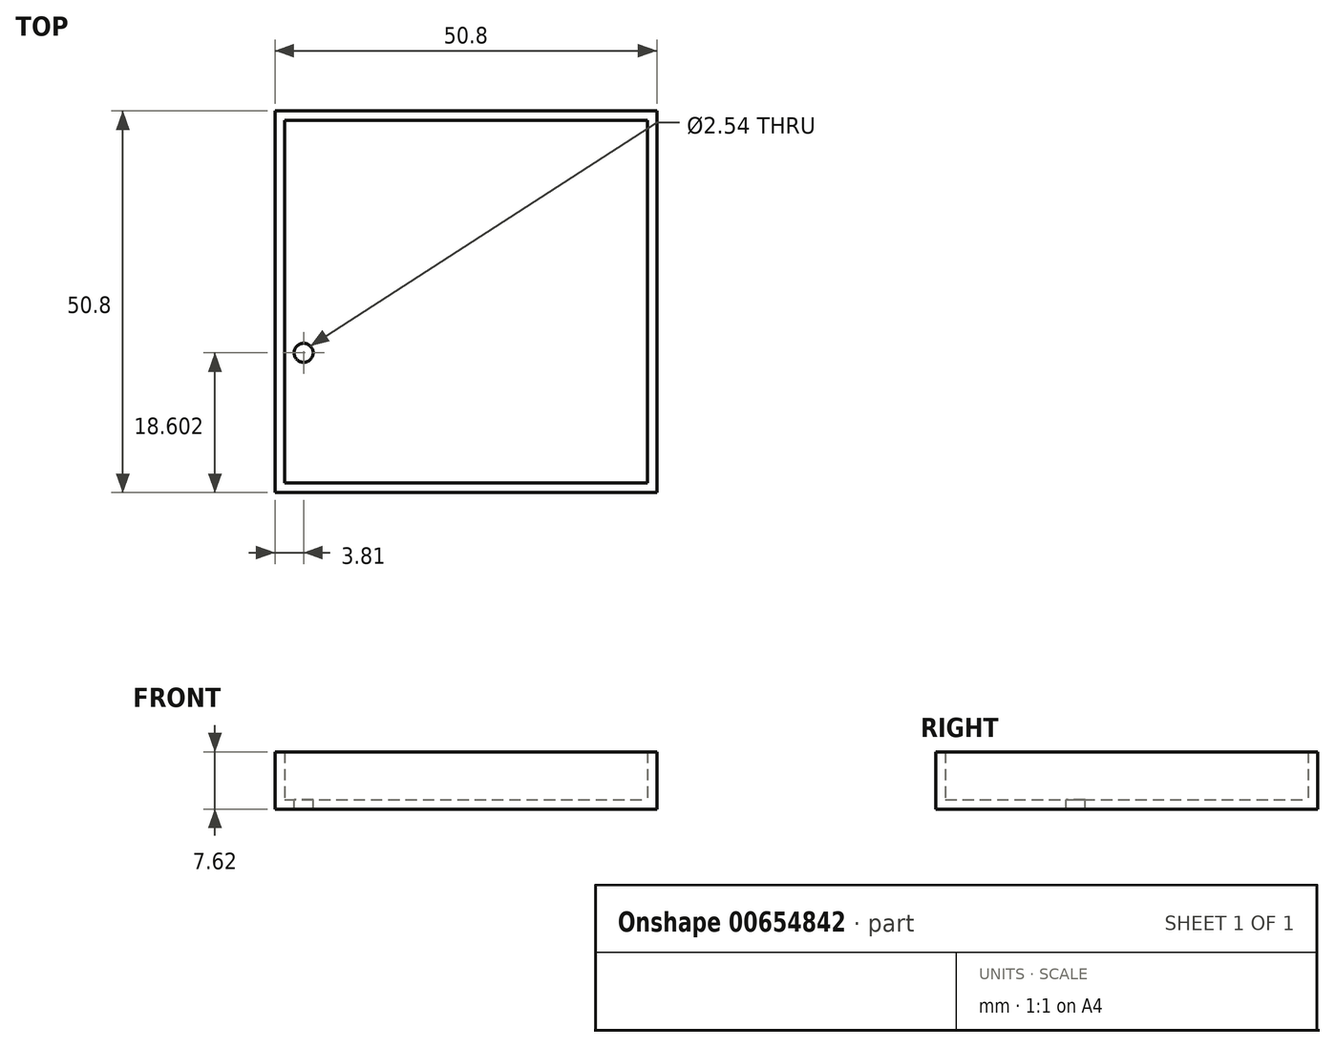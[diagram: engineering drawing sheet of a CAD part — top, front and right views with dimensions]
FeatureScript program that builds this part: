
annotation { "Feature Type Name" : "Feature", "Feature Type Description" : "" }
export const myFeature = defineFeature(function(context is Context, id is Id, definition is map)
    precondition{}
    {
        {
            var Q0;
            Q0=qCreatedBy(makeId("Top.planeOp"),FACE);
            var sketch = newSketch(context, id + "F0", { "sketchPlane" : qUnion([Q0])});
            skLineSegment(sketch, "E0.bottom", {"start": v(0, 0) * mm, "end": v(50.8, 0) * mm});
            skLineSegment(sketch, "E0.top", {"start": v(0, 50.8) * mm, "end": v(50.8, 50.8) * mm});
            skLineSegment(sketch, "E0.left", {"start": v(0, 0) * mm, "end": v(0, 50.8) * mm});
            skLineSegment(sketch, "E0.right", {"start": v(50.8, 0) * mm, "end": v(50.8, 50.8) * mm});
            skSolve(sketch);
        }
        {
            var Q0;
            Q0 = qSketchRegion(id + "F0", true);
            extrude(context, id + "F1", {"entities" : qUnion([Q0]), "depth" : 7.62 * mm, "offsetDistance" : 25.4 * mm});
        }
        {
            var Q0;
            Q0=makeQuery(id+"F1.opExtrude","CAP_FACE",FACE,{"disambiguationData":[OSD([sQuery(id+"F0.wireOp",EDGE,"E0.bottom"),sQuery(id+"F0.wireOp",EDGE,"E0.top"),sQuery(id+"F0.wireOp",EDGE,"E0.left"),sQuery(id+"F0.wireOp",EDGE,"E0.right")])],"isStart":false});
            shell(context, id + "F2", {"entities" : qUnion([Q0]), "thickness" : 1.27 * mm});
        }
        {
            var Q0;
            Q0=makeQuery(id+"F2.opShell","OFFSET_FACE",FACE,{"disambiguationData":[OSD([sQuery(id+"F0.wireOp",EDGE,"E0.bottom"),sQuery(id+"F0.wireOp",EDGE,"E0.top"),sQuery(id+"F0.wireOp",EDGE,"E0.left"),sQuery(id+"F0.wireOp",EDGE,"E0.right")])]});
            var sketch = newSketch(context, id + "F3", { "sketchPlane" : qUnion([Q0])});
            skLineSegment(sketch, "E1", {"start": v(1.27, 11.52) * mm, "end": v(6.35, 11.52) * mm});
            skLineSegment(sketch, "E2", {"start": v(6.35, 11.52) * mm, "end": v(6.35, 39.6) * mm});
            skLineSegment(sketch, "E3", {"start": v(6.35, 39.6) * mm, "end": v(14.23, 39.6) * mm});
            skLineSegment(sketch, "E4", {"start": v(14.23, 39.6) * mm, "end": v(14.23, 23.52) * mm});
            skLineSegment(sketch, "E5", {"start": v(14.23, 23.52) * mm, "end": v(31.1, 23.52) * mm});
            skLineSegment(sketch, "E6", {"start": v(33.7, 19.63) * mm, "end": v(33.7, 14.11) * mm});
            skArc(sketch, "E7", {"start": v(33.7, 19.63) * mm, "mid": v(33, 21.97) * mm, "end": v(31.1, 23.52) * mm});
            skCircle(sketch, "E8", {"center": v(3.81, 18.6) * mm, "radius": 1.27 * mm});
            skPoint(sketch, "E8.centerSnap0", {"position": v(3.81, 11.52) * mm});
            skSolve(sketch);
        }
        {
            var Q0;
            Q0 = qSketchRegion(id + "F3", true);
            extrude(context, id + "F4", {"entities" : qUnion([Q0]), "operationType" : NewBodyOperationType.REMOVE, "oppositeDirection" : true, "depth" : 25.4 * mm, "offsetDistance" : 25.4 * mm});
        }
    });
